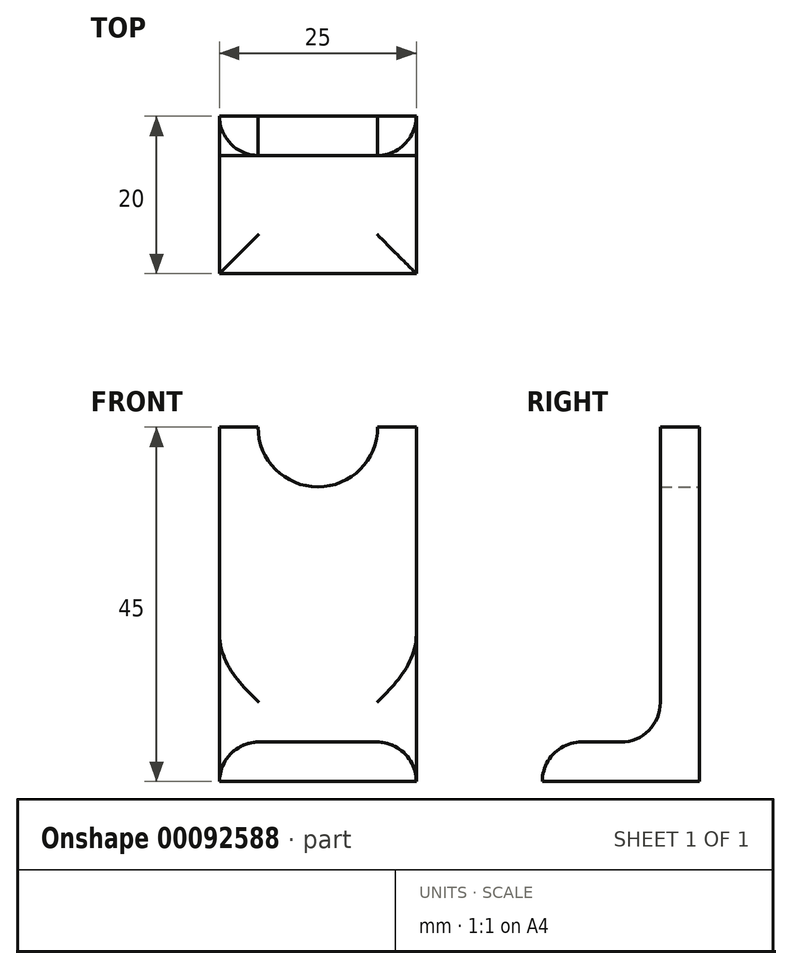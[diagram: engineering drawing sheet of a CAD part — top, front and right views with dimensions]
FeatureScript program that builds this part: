
annotation { "Feature Type Name" : "Feature", "Feature Type Description" : "" }
export const myFeature = defineFeature(function(context is Context, id is Id, definition is map)
    precondition{}
    {
        {
            var Q0;
            Q0=qCreatedBy(makeId("Front.planeOp"),FACE);
            var sketch = newSketch(context, id + "F0", { "sketchPlane" : qUnion([Q0])});
            skLineSegment(sketch, "E0.bottom", {"start": v(12.5, -22.5) * mm, "end": v(-12.5, -22.5) * mm});
            skLineSegment(sketch, "E0.top", {"start": v(12.5, 22.5) * mm, "end": v(-12.5, 22.5) * mm});
            skLineSegment(sketch, "E0.left", {"start": v(12.5, -22.5) * mm, "end": v(12.5, 22.5) * mm});
            skLineSegment(sketch, "E0.right", {"start": v(-12.5, -22.5) * mm, "end": v(-12.5, 22.5) * mm});
            skPoint(sketch, "E0.middle", {"position": v(0, 0) * mm});
            skCircle(sketch, "E1", {"center": v(0, 22.5) * mm, "radius": 7.6 * mm});
            skSolve(sketch);
        }
        {
            var Q0;
            Q0=makeQuery(id+"F0.imprint","IMPRINT",FACE,{"disambiguationData":[TD([[makeQuery(id+"F0.imprint","IMPRINT",EDGE,{"derivedFrom":sQuery(id+"F0.wireOp",EDGE,"E0.bottom")}),-1.0]])]});
            extrude(context, id + "F1", {"entities" : qUnion([Q0]), "depth" : 5 * mm});
        }
        {
            var Q0;
            Q0=makeQuery(id+"F1.opExtrude","CAP_FACE",FACE,{"disambiguationData":[OSD([sQuery(id+"F0.wireOp",EDGE,"E0.bottom"),sQuery(id+"F0.wireOp",EDGE,"E0.top"),sQuery(id+"F0.wireOp",EDGE,"E0.left"),sQuery(id+"F0.wireOp",EDGE,"E0.right"),sQuery(id+"F0.wireOp",EDGE,"E1")])],"isStart":false});
            var sketch = newSketch(context, id + "F2", { "sketchPlane" : qUnion([Q0])});
            skLineSegment(sketch, "E2.bottom", {"start": v(-12.5, -22.5) * mm, "end": v(12.5, -22.5) * mm});
            skLineSegment(sketch, "E2.top", {"start": v(-12.5, -17.5) * mm, "end": v(12.5, -17.5) * mm});
            skLineSegment(sketch, "E2.left", {"start": v(-12.5, -22.5) * mm, "end": v(-12.5, -17.5) * mm});
            skLineSegment(sketch, "E2.right", {"start": v(12.5, -22.5) * mm, "end": v(12.5, -17.5) * mm});
            skSolve(sketch);
        }
        {
            var Q0;
            Q0=makeQuery(id+"F2.imprint","IMPRINT",FACE,{"disambiguationData":[TD([[makeQuery(id+"F2.imprint","IMPRINT",EDGE,{"derivedFrom":sQuery(id+"F2.wireOp",EDGE,"E2.bottom")}),-1.0]])]});
            extrude(context, id + "F3", {"entities" : qUnion([Q0]), "operationType" : NewBodyOperationType.ADD, "depth" : 15 * mm});
        }
        {
            var Q0;
            Q0=makeQuery(id+"F3.opExtrude","SWEPT_FACE",FACE,{"disambiguationData":[OSD([sQuery(id+"F2.wireOp",EDGE,"E2.top")])]});
            fillet(context, id + "F4", {"entities" : qUnion([Q0]), "radius" : 5 * mm, "tangentPropagation" : true, "allowEdgeOverflow" : false});
        }
    });
